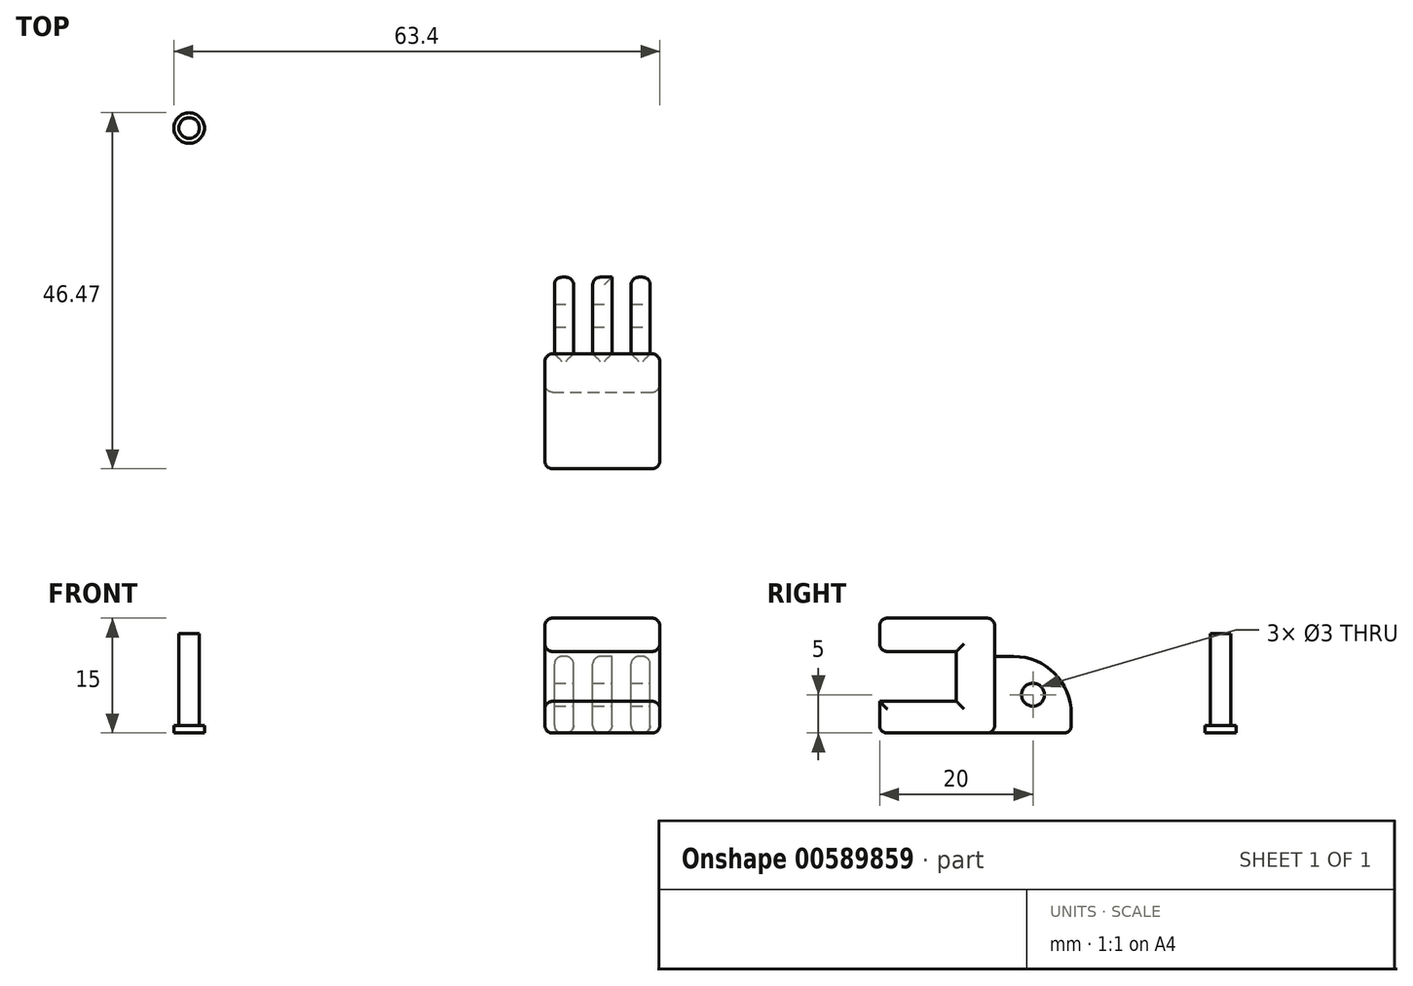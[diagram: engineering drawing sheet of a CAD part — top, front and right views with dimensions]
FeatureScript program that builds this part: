
annotation { "Feature Type Name" : "Feature", "Feature Type Description" : "" }
export const myFeature = defineFeature(function(context is Context, id is Id, definition is map)
    precondition{}
    {
        {
            var Q0;
            Q0=qCreatedBy(makeId("Top.planeOp"),FACE);
            var sketch = newSketch(context, id + "F0", { "sketchPlane" : qUnion([Q0])});
            skLineSegment(sketch, "E0.bottom", {"start": v(7.5, -7.5) * mm, "end": v(-7.5, -7.5) * mm});
            skLineSegment(sketch, "E0.top", {"start": v(7.5, 7.5) * mm, "end": v(-7.5, 7.5) * mm});
            skLineSegment(sketch, "E0.left", {"start": v(7.5, -7.5) * mm, "end": v(7.5, 7.5) * mm});
            skLineSegment(sketch, "E0.right", {"start": v(-7.5, -7.5) * mm, "end": v(-7.5, 7.5) * mm});
            skPoint(sketch, "E0.middle", {"position": v(0, 0) * mm});
            skCircle(sketch, "E1", {"center": v(-53.9, 36.97) * mm, "radius": 2 * mm});
            skCircle(sketch, "E2", {"center": v(-53.9, 36.97) * mm, "radius": 1.35 * mm});
            skSolve(sketch);
        }
        {
            var Q0;
            Q0=makeQuery(id+"F0.imprint","IMPRINT",FACE,{"disambiguationData":[TD([[makeQuery(id+"F0.imprint","IMPRINT",EDGE,{"derivedFrom":sQuery(id+"F0.wireOp",EDGE,"E0.bottom")}),-1.0]])]});
            extrude(context, id + "F1", {"entities" : qUnion([Q0]), "depth" : 15 * mm, "offsetDistance" : 25 * mm});
        }
        {
            var Q0;
            Q0=makeQuery(id+"F1.opExtrude","SWEPT_FACE",FACE,{"disambiguationData":[OSD([sQuery(id+"F0.wireOp",EDGE,"E0.bottom")])]});
            var sketch = newSketch(context, id + "F2", { "sketchPlane" : qUnion([Q0])});
            skLineSegment(sketch, "E3.bottom", {"start": v(-7.5, 10.65) * mm, "end": v(7.5, 10.65) * mm});
            skLineSegment(sketch, "E3.top", {"start": v(-7.5, 4.15) * mm, "end": v(7.5, 4.15) * mm});
            skLineSegment(sketch, "E3.left", {"start": v(-7.5, 10.65) * mm, "end": v(-7.5, 4.15) * mm});
            skLineSegment(sketch, "E3.right", {"start": v(7.5, 10.65) * mm, "end": v(7.5, 4.15) * mm});
            skLineSegment(sketch, "E4", {"start": v(8.28, 7.4) * mm, "end": v(-8.34, 7.4) * mm, "construction": true});
            skPoint(sketch, "E4.startSnap0", {"position": v(-7.5, 7.4) * mm});
            skSolve(sketch);
        }
        {
            var Q0;
            Q0=makeQuery(id+"F2.imprint","IMPRINT",FACE,{"disambiguationData":[TD([[makeQuery(id+"F2.imprint","IMPRINT",EDGE,{"derivedFrom":sQuery(id+"F2.wireOp",EDGE,"E3.bottom")}),-1.0]])]});
            var Q1;
            Q1=makeQuery(id+"F1.opExtrude","SWEPT_FACE",FACE,{"disambiguationData":[OSD([sQuery(id+"F0.wireOp",EDGE,"E0.top")])]});
            extrude(context, id + "F3", {"entities" : qUnion([Q0, Q1]), "operationType" : NewBodyOperationType.REMOVE, "oppositeDirection" : true, "depth" : 10 * mm, "offsetDistance" : 25 * mm});
        }
        {
            var Q0;
            Q0=makeQuery(id+"F1.opExtrude","SWEPT_FACE",FACE,{"disambiguationData":[OSD([sQuery(id+"F0.wireOp",EDGE,"E0.top")])]});
            var sketch = newSketch(context, id + "F4", { "sketchPlane" : qUnion([Q0])});
            skLineSegment(sketch, "E5.bottom", {"start": v(-1.25, 0) * mm, "end": v(1.25, 0) * mm});
            skLineSegment(sketch, "E5.top", {"start": v(-1.25, 10) * mm, "end": v(1.25, 10) * mm});
            skLineSegment(sketch, "E5.left", {"start": v(-1.25, 0) * mm, "end": v(-1.25, 10) * mm});
            skLineSegment(sketch, "E5.right", {"start": v(1.25, 0) * mm, "end": v(1.25, 10) * mm});
            skLineSegment(sketch, "E6.bottom", {"start": v(-6.25, 0) * mm, "end": v(-3.75, 0) * mm});
            skLineSegment(sketch, "E6.top", {"start": v(-6.25, 10) * mm, "end": v(-3.75, 10) * mm});
            skLineSegment(sketch, "E6.left", {"start": v(-6.25, 0) * mm, "end": v(-6.25, 10) * mm});
            skLineSegment(sketch, "E6.right", {"start": v(-3.75, 0) * mm, "end": v(-3.75, 10) * mm});
            skLineSegment(sketch, "E7.bottom", {"start": v(3.75, 0) * mm, "end": v(6.25, 0) * mm});
            skLineSegment(sketch, "E7.top", {"start": v(3.75, 10) * mm, "end": v(6.25, 10) * mm});
            skLineSegment(sketch, "E7.left", {"start": v(3.75, 0) * mm, "end": v(3.75, 10) * mm});
            skLineSegment(sketch, "E7.right", {"start": v(6.25, 0) * mm, "end": v(6.25, 10) * mm});
            skSolve(sketch);
        }
        {
            var Q0;
            Q0=makeQuery(id+"F4.imprint","IMPRINT",FACE,{"disambiguationData":[TD([[makeQuery(id+"F4.imprint","IMPRINT",EDGE,{"derivedFrom":sQuery(id+"F4.wireOp",EDGE,"E6.bottom")}),1.0]])]});
            var Q1;
            Q1=makeQuery(id+"F4.imprint","IMPRINT",FACE,{"disambiguationData":[TD([[makeQuery(id+"F4.imprint","IMPRINT",EDGE,{"derivedFrom":sQuery(id+"F4.wireOp",EDGE,"E5.bottom")}),1.0]])]});
            var Q2;
            Q2=makeQuery(id+"F4.imprint","IMPRINT",FACE,{"disambiguationData":[TD([[makeQuery(id+"F4.imprint","IMPRINT",EDGE,{"derivedFrom":sQuery(id+"F4.wireOp",EDGE,"E7.bottom")}),1.0]])]});
            extrude(context, id + "F5", {"entities" : qUnion([Q0, Q1, Q2]), "operationType" : NewBodyOperationType.ADD, "depth" : 10 * mm, "offsetDistance" : 25 * mm});
        }
        {
            var Q0;
            Q0=makeQuery(id+"F5.opExtrude","SWEPT_FACE",FACE,{"disambiguationData":[OSD([sQuery(id+"F4.wireOp",EDGE,"E6.left")])]});
            var sketch = newSketch(context, id + "F6", { "sketchPlane" : qUnion([Q0])});
            skCircle(sketch, "E8", {"center": v(12.5, 5) * mm, "radius": 1.5 * mm});
            skPoint(sketch, "E8.centerSnap0", {"position": v(17.5, 5) * mm});
            skPoint(sketch, "E8.centerSnap1", {"position": v(12.5, 10) * mm});
            skSolve(sketch);
        }
        {
            var Q0;
            Q0=makeQuery(id+"F6.imprint","IMPRINT",FACE,{"disambiguationData":[TD([[makeQuery(id+"F6.imprint","IMPRINT",EDGE,{"derivedFrom":sQuery(id+"F6.wireOp",EDGE,"E8")}),1.0]])]});
            extrude(context, id + "F7", {"entities" : qUnion([Q0]), "operationType" : NewBodyOperationType.REMOVE, "endBound" : BoundingType.THROUGH_ALL, "oppositeDirection" : true, "depth" : 25 * mm, "offsetDistance" : 25 * mm});
        }
        {
            var Q0;
            Q0=makeQuery(id+"F5.opExtrude","CAP_EDGE",EDGE,{"disambiguationData":[OSD([sQuery(id+"F4.wireOp",EDGE,"E6.top")])],"isStart":false});
            var Q1;
            Q1=makeQuery(id+"F5.opExtrude","CAP_EDGE",EDGE,{"disambiguationData":[OSD([sQuery(id+"F4.wireOp",EDGE,"E5.top")])],"isStart":false});
            var Q2;
            Q2=makeQuery(id+"F5.opExtrude","CAP_EDGE",EDGE,{"disambiguationData":[OSD([sQuery(id+"F4.wireOp",EDGE,"E7.top")])],"isStart":false});
            fillet(context, id + "F8", {"entities" : qUnion([Q0, Q1, Q2]), "radius" : 7.5 * mm, "tangentPropagation" : true, "allowEdgeOverflow" : false});
        }
        {
            var Q0;
            Q0=makeQuery(id+"F3.boolean.opBoolean","COPY",EDGE,{"derivedFrom":makeQuery(id+"F3.opExtrude","CAP_EDGE",EDGE,{"disambiguationData":[OSD([sQuery(id+"F2.wireOp",EDGE,"E3.bottom")])],"isStart":true})});
            var Q1;
            Q1=makeQuery(id+"F3.boolean.opBoolean","COPY",EDGE,{"derivedFrom":makeQuery(id+"F3.opExtrude","CAP_EDGE",EDGE,{"disambiguationData":[OSD([sQuery(id+"F2.wireOp",EDGE,"E3.top")])],"isStart":true})});
            var Q2;
            Q2=makeQuery(id+"F3.boolean.opBoolean","COPY",EDGE,{"derivedFrom":makeQuery(id+"F3.opExtrude","SWEPT_EDGE",EDGE,{"disambiguationData":[OSD([sQuery(id+"F0.wireOp",EDGE,"E0.bottom"),sQuery(id+"F0.wireOp",EDGE,"E0.left"),sQuery(id+"F2.wireOp",EDGE,"E3.top"),sQuery(id+"F2.wireOp",EDGE,"E3.right")])]})});
            var Q3;
            Q3=makeQuery(id+"F3.boolean.opBoolean","COPY",EDGE,{"derivedFrom":makeQuery(id+"F3.opExtrude","SWEPT_EDGE",EDGE,{"disambiguationData":[OSD([sQuery(id+"F0.wireOp",EDGE,"E0.bottom"),sQuery(id+"F0.wireOp",EDGE,"E0.left"),sQuery(id+"F2.wireOp",EDGE,"E3.bottom"),sQuery(id+"F2.wireOp",EDGE,"E3.right")])]})});
            var Q4;
            Q4=makeQuery(id+"F1.opExtrude","SWEPT_FACE",FACE,{"disambiguationData":[OSD([sQuery(id+"F0.wireOp",EDGE,"E0.left")])]});
            var Q5;
            Q5=makeQuery(id+"F1.opExtrude","SWEPT_FACE",FACE,{"disambiguationData":[OSD([sQuery(id+"F0.wireOp",EDGE,"E0.right")])]});
            var Q6;
            Q6=makeQuery(id+"F1.opExtrude","CAP_FACE",FACE,{"disambiguationData":[OSD([sQuery(id+"F0.wireOp",EDGE,"E0.bottom"),sQuery(id+"F0.wireOp",EDGE,"E0.top"),sQuery(id+"F0.wireOp",EDGE,"E0.left"),sQuery(id+"F0.wireOp",EDGE,"E0.right")])],"isStart":false});
            var Q7;
            Q7=makeQuery(id+"F5.boolean.opBoolean","MERGE",FACE,{"derivedFrom":[makeQuery(id+"F1.opExtrude","CAP_FACE",FACE,{"disambiguationData":[OSD([sQuery(id+"F0.wireOp",EDGE,"E0.bottom"),sQuery(id+"F0.wireOp",EDGE,"E0.top"),sQuery(id+"F0.wireOp",EDGE,"E0.left"),sQuery(id+"F0.wireOp",EDGE,"E0.right")])],"isStart":true}),makeQuery(id+"F5.opExtrude","SWEPT_FACE",FACE,{"disambiguationData":[OSD([sQuery(id+"F4.wireOp",EDGE,"E5.bottom")])]}),makeQuery(id+"F5.opExtrude","SWEPT_FACE",FACE,{"disambiguationData":[OSD([sQuery(id+"F4.wireOp",EDGE,"E6.bottom")])]}),makeQuery(id+"F5.opExtrude","SWEPT_FACE",FACE,{"disambiguationData":[OSD([sQuery(id+"F4.wireOp",EDGE,"E7.bottom")])]})]});
            var Q8;
            Q8=makeQuery(id+"F8.opFillet","BLEND_FACE",FACE,{"disambiguationData":[OSD([sQuery(id+"F4.wireOp",EDGE,"E6.top")])]});
            var Q9;
            Q9=makeQuery(id+"F8.opFillet","BLEND_EDGE",EDGE,{"blendedFrom":[makeQuery(id+"F5.opExtrude","CAP_EDGE",EDGE,{"disambiguationData":[OSD([sQuery(id+"F4.wireOp",EDGE,"E5.top")])],"isStart":false}),makeQuery(id+"F5.opExtrude","SWEPT_FACE",FACE,{"disambiguationData":[OSD([sQuery(id+"F4.wireOp",EDGE,"E5.right")])]})],"blendedInto":[makeQuery(id+"F5.opExtrude","SWEPT_FACE",FACE,{"disambiguationData":[OSD([sQuery(id+"F4.wireOp",EDGE,"E5.right")])]})]});
            var Q10;
            Q10=makeQuery(id+"F8.opFillet","BLEND_FACE",FACE,{"disambiguationData":[OSD([sQuery(id+"F4.wireOp",EDGE,"E7.top")])]});
            fillet(context, id + "F9", {"entities" : qUnion([Q0, Q1, Q2, Q3, Q4, Q5, Q6, Q7, Q8, Q9, Q10]), "radius" : 1 * mm, "tangentPropagation" : true, "allowEdgeOverflow" : false});
        }
        {
            var Q0;
            Q0=makeQuery(id+"F0.imprint","IMPRINT",FACE,{"disambiguationData":[TD([[makeQuery(id+"F0.imprint","IMPRINT",EDGE,{"derivedFrom":sQuery(id+"F0.wireOp",EDGE,"E2")}),1.0]])]});
            extrude(context, id + "F10", {"entities" : qUnion([Q0]), "depth" : 13 * mm, "offsetDistance" : 25 * mm});
        }
        {
            var Q0;
            Q0=makeQuery(id+"F0.imprint","IMPRINT",FACE,{"disambiguationData":[TD([[makeQuery(id+"F0.imprint","IMPRINT",EDGE,{"derivedFrom":sQuery(id+"F0.wireOp",EDGE,"E1")}),1.0]])]});
            extrude(context, id + "F11", {"entities" : qUnion([Q0]), "operationType" : NewBodyOperationType.ADD, "depth" : 1 * mm, "offsetDistance" : 25 * mm});
        }
    });
